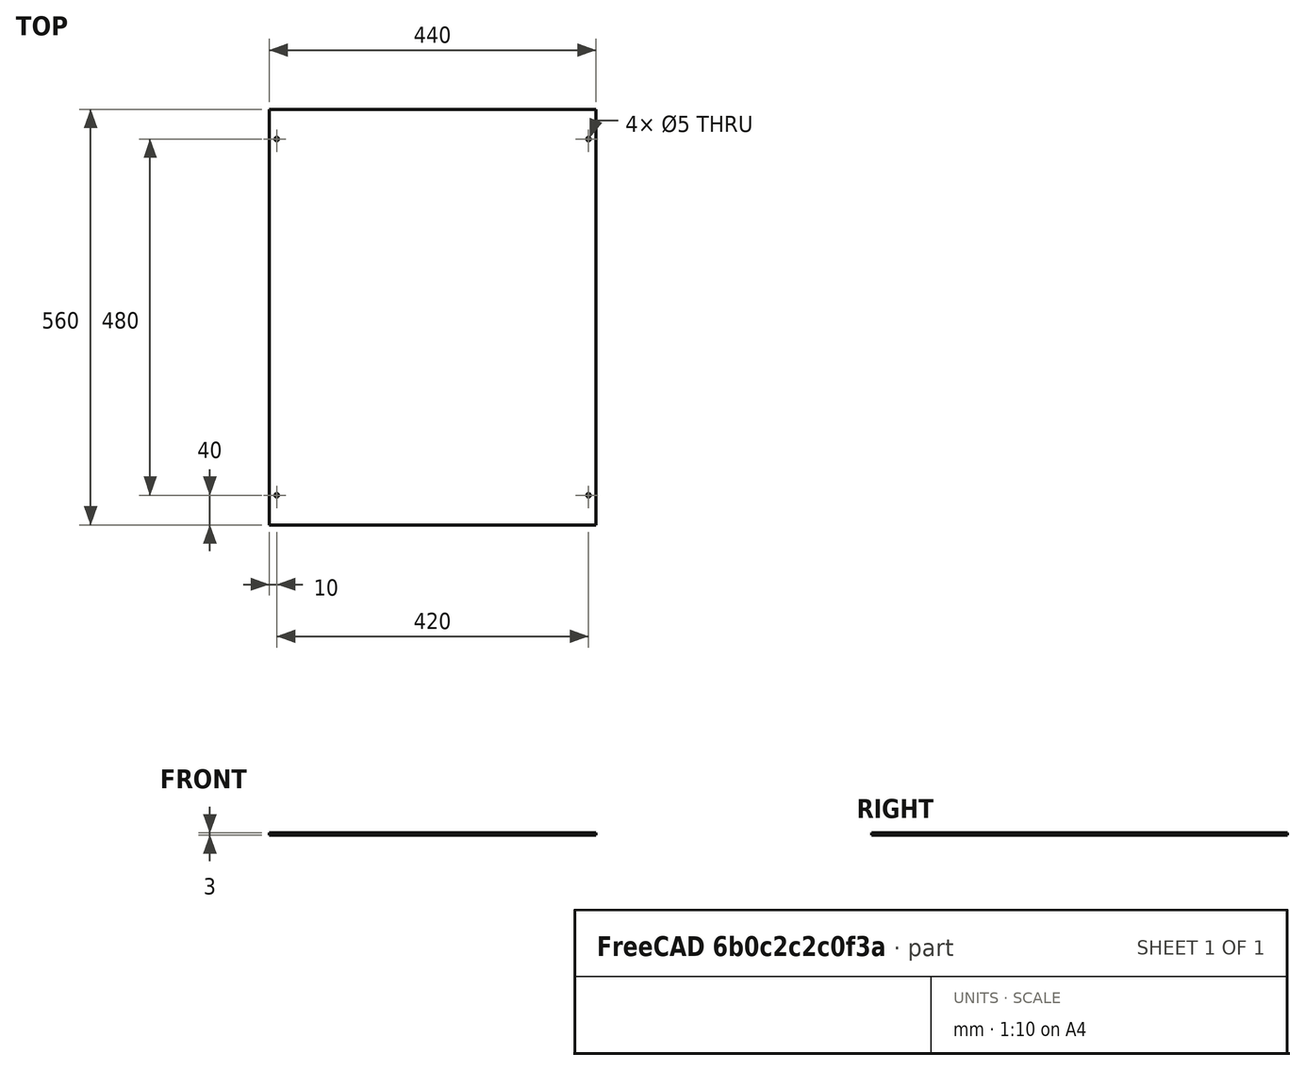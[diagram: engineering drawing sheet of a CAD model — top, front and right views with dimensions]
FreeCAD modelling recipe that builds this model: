
FCSTD DOCUMENT  (FreeCAD 1.0R38641 +468 (Git))
Label: plate_side
License: All rights reserved
LicenseURL: https://en.wikipedia.org/wiki/All_rights_reserved
objects: TechDraw::DrawViewDimension×7, Sketcher::SketchObject×1, PartDesign::Pad×1, PartDesign::Body×1, TechDraw::DrawSVGTemplate×1, TechDraw::DrawProjGroupItem×1, TechDraw::DrawProjGroup×1, TechDraw::DrawPage×1
note: 17 computed .brp shape members not serialized (recipe doc carries the construction recipe); baked Part::Feature solids carry a one-line shape summary decoded from their .brp

FEATURE [Sketcher::SketchObject] Sketch
  ArcFitTolerance = 1e-06
  AttachmentSupport = -> [XY_Plane001]
  FullyConstrained = true
  MakeInternals = false
  MapMode = 5
  sketch-geometry (9):
    g0: LineSegment StartX=-220 StartY=280 StartZ=0 EndX=-220 EndY=-280 EndZ=0
    g1: LineSegment StartX=-220 StartY=-280 StartZ=0 EndX=220 EndY=-280 EndZ=0
    g2: LineSegment StartX=220 StartY=-280 StartZ=0 EndX=220 EndY=280 EndZ=0
    g3: LineSegment StartX=220 StartY=280 StartZ=0 EndX=-220 EndY=280 EndZ=0
    g4: GeomPoint [constr] X=0 Y=0 Z=0
    g5: Circle CenterX=-210 CenterY=240 CenterZ=0 NormalX=0 NormalY=0 NormalZ=1 AngleXU=0 Radius=2.5
    g6: Circle CenterX=210 CenterY=240 CenterZ=0 NormalX=0 NormalY=0 NormalZ=1 AngleXU=0 Radius=2.5
    g7: Circle CenterX=-210 CenterY=-240 CenterZ=0 NormalX=0 NormalY=0 NormalZ=1 AngleXU=0 Radius=2.5
    g8: Circle CenterX=210 CenterY=-240 CenterZ=0 NormalX=0 NormalY=0 NormalZ=1 AngleXU=0 Radius=2.5
  constraints (21):
    c: Coincident(g0,g1)
    c: Coincident(g1,g2)
    c: Coincident(g2,g3)
    c: Coincident(g3,g0)
    c: Vertical(g0)
    c: Vertical(g2)
    c: Horizontal(g1)
    c: Horizontal(g3)
    c: Symmetric(g2,g0,g4)
    c: Coincident(g4,g-1)
    c: DistanceX(g1,g1) = 440
    c: Distance(g0,g0) = 560
    c: Symmetric(g7,g8,g-2)
    c: Symmetric(g5,g6,g-2)
    c: Equal(g5,g6)
    c: Equal(g6,g7)
    c: Equal(g7,g8)
    c: Diameter(g5) = 5
    c: DistanceX(g5,g6) = 420
    c: Distance(g5,g3) = 40
    c: Symmetric(g7,g5,g-1)
FEATURE [PartDesign::Pad] Pad
  Direction = (0,0,1)
  Length = 3
  Length2 = 10
  Profile = -> Sketch
  ReferenceAxis = -> Sketch [N_Axis]
  Refine = true
  Suppressed = false
  Type = 0
FEATURE [PartDesign::Body] Body001  label="plate_side"
  AllowCompound = false
  Group = -> [Sketch,Pad]
  Origin = -> Origin001
  Tip = -> Pad
FEATURE [TechDraw::DrawSVGTemplate] Template
  EditableTexts = approval_person=B. Hecate; creator=Djordje Vujic; date_of_issue=20.1.25.; document_type=Assembly Drawing; general_tolerances=ISO 2768-m; identification_number=DN; language_code=EN; part_material=Stainless steel Mat.No. 1.4301; revision_index=AAA; sheet_number=1 / 2; sheet_scale=1 : 3; title=plate_side
  Height = 297
  Orientation = 0
  Template = /snap/freecad/1248/usr/share/Mod/TechDraw/Templates/A4_Portrait_ISO5457_minimal.svg
  Width = 210
FEATURE [TechDraw::DrawProjGroupItem] ProjItem  label="Front"
  CoarseView = false
  Direction = (0,0,1)
  Focus = 100
  HardHidden = false
  IsoCount = 0
  IsoHidden = false
  IsoVisible = false
  LockPosition = true
  Perspective = false
  Rotation = 0
  RotationVector = (1,0,0)
  Scale = 0.333333
  ScaleType = 0
  ScrubCount = 1
  SeamHidden = false
  SeamVisible = false
  SmoothHidden = false
  SmoothVisible = true
  Source = -> [Pad]
  Type = 0
  X = 0
  XDirection = (1,0,0)
  Y = 0
FEATURE [TechDraw::DrawProjGroup] ProjGroup
  Anchor = -> ProjItem
  AutoDistribute = true
  LockPosition = false
  ProjectionType = 0
  Rotation = 0
  Scale = 0.333333
  ScaleType = 2
  Source = -> [Pad]
  Views = -> [ProjItem]
  X = 112.185
  Y = 167.732
  spacingX = 15
  spacingY = 15
FEATURE [TechDraw::DrawViewDimension] Dimension
  AngleOverride = false
  Arbitrary = false
  ArbitraryTolerances = false
  BoxCorners = (2) [(-73.3333,-93.3332,0),(73.3333,93.3332,0)]
  EqualTolerance = true
  ExtensionAngle = 0
  FormatSpec = %.2w
  FormatSpecOverTolerance = %+.2w
  FormatSpecUnderTolerance = %+.2w
  Inverted = false
  LineAngle = 0
  LockPosition = false
  MeasureType = 1
  OverTolerance = 0
  References2D = -> [ProjItem]
  Rotation = 0
  ScaleType = 0
  TheoreticalExact = false
  Type = 2
  UnderTolerance = 0
  X = -85.4097
  Y = 5.18089
FEATURE [TechDraw::DrawViewDimension] Dimension001
  AngleOverride = false
  Arbitrary = false
  ArbitraryTolerances = false
  BoxCorners = (2) [(-73.3333,-93.3332,0),(73.3333,93.3332,0)]
  EqualTolerance = true
  ExtensionAngle = 0
  FormatSpec = %.2w
  FormatSpecOverTolerance = %+.2w
  FormatSpecUnderTolerance = %+.2w
  Inverted = false
  LineAngle = 0
  LockPosition = false
  MeasureType = 1
  OverTolerance = 0
  References2D = -> [ProjItem]
  Rotation = 0
  ScaleType = 0
  TheoreticalExact = false
  Type = 0
  UnderTolerance = 0
  X = -56.3812
  Y = 3.94419
FEATURE [TechDraw::DrawViewDimension] Dimension002
  AngleOverride = false
  Arbitrary = false
  ArbitraryTolerances = false
  BoxCorners = (2) [(-73.3333,-93.3332,0),(73.3333,93.3332,0)]
  EqualTolerance = true
  ExtensionAngle = 0
  FormatSpec = %.2w
  FormatSpecOverTolerance = %+.2w
  FormatSpecUnderTolerance = %+.2w
  Inverted = false
  LineAngle = 0
  LockPosition = false
  MeasureType = 1
  OverTolerance = 0
  References2D = -> [ProjItem]
  Rotation = 0
  ScaleType = 0
  TheoreticalExact = false
  Type = 1
  UnderTolerance = 0
  X = -3.05848
  Y = 105.234
FEATURE [TechDraw::DrawViewDimension] Dimension003
  AngleOverride = false
  Arbitrary = false
  ArbitraryTolerances = false
  BoxCorners = (2) [(-73.3333,-93.3332,0),(73.3333,93.3332,0)]
  EqualTolerance = true
  ExtensionAngle = 0
  FormatSpec = %.2w
  FormatSpecOverTolerance = %+.2w
  FormatSpecUnderTolerance = %+.2w
  Inverted = false
  LineAngle = 0
  LockPosition = false
  MeasureType = 1
  OverTolerance = 0
  References2D = -> [ProjItem]
  Rotation = 0
  ScaleType = 0
  TheoreticalExact = false
  Type = 0
  UnderTolerance = 0
  X = 80.5803
  Y = 73.8387
FEATURE [TechDraw::DrawViewDimension] Dimension004
  AngleOverride = false
  Arbitrary = false
  ArbitraryTolerances = false
  BoxCorners = (2) [(-73.3333,-93.3332,0),(73.3333,93.3332,0)]
  EqualTolerance = true
  ExtensionAngle = 0
  FormatSpec = %.2w
  FormatSpecOverTolerance = %+.2w
  FormatSpecUnderTolerance = %+.2w
  Inverted = false
  LineAngle = 0
  LockPosition = false
  MeasureType = 1
  OverTolerance = 0
  References2D = -> [ProjItem]
  Rotation = 0
  ScaleType = 0
  TheoreticalExact = false
  Type = 0
  UnderTolerance = 0
  X = -56.3813
  Y = 86.6666
FEATURE [TechDraw::DrawViewDimension] Dimension005
  AngleOverride = false
  Arbitrary = false
  ArbitraryTolerances = false
  BoxCorners = (2) [(-73.3333,-93.3332,0),(73.3333,93.3332,0)]
  EqualTolerance = true
  ExtensionAngle = 0
  FormatSpec = ⌀%.2w
  FormatSpecOverTolerance = %+.2w
  FormatSpecUnderTolerance = %+.2w
  Inverted = false
  LineAngle = 0
  LockPosition = false
  MeasureType = 1
  OverTolerance = 0
  References2D = -> [ProjItem]
  Rotation = 0
  ScaleType = 0
  TheoreticalExact = false
  Type = 5
  UnderTolerance = 0
  X = 69.6314
  Y = -65.9903
FEATURE [TechDraw::DrawViewDimension] Dimension006
  AngleOverride = false
  Arbitrary = false
  ArbitraryTolerances = false
  BoxCorners = (2) [(-73.3333,-93.3332,0),(73.3333,93.3332,0)]
  EqualTolerance = true
  ExtensionAngle = 0
  FormatSpec = %.2w
  FormatSpecOverTolerance = %+.2w
  FormatSpecUnderTolerance = %+.2w
  Inverted = false
  LineAngle = 0
  LockPosition = false
  MeasureType = 1
  OverTolerance = 0
  References2D = -> [ProjItem]
  Rotation = 0
  ScaleType = 0
  TheoreticalExact = false
  Type = 0
  UnderTolerance = 0
  X = 0
  Y = -84.7541
FEATURE [TechDraw::DrawPage] Page
  KeepUpdated = true
  NextBalloonIndex = 1
  ProjectionType = 0
  Template = -> Template
  Views = -> [ProjGroup,Dimension,Dimension001,Dimension002,Dimension003,Dimension004,Dimension005,Dimension006]
